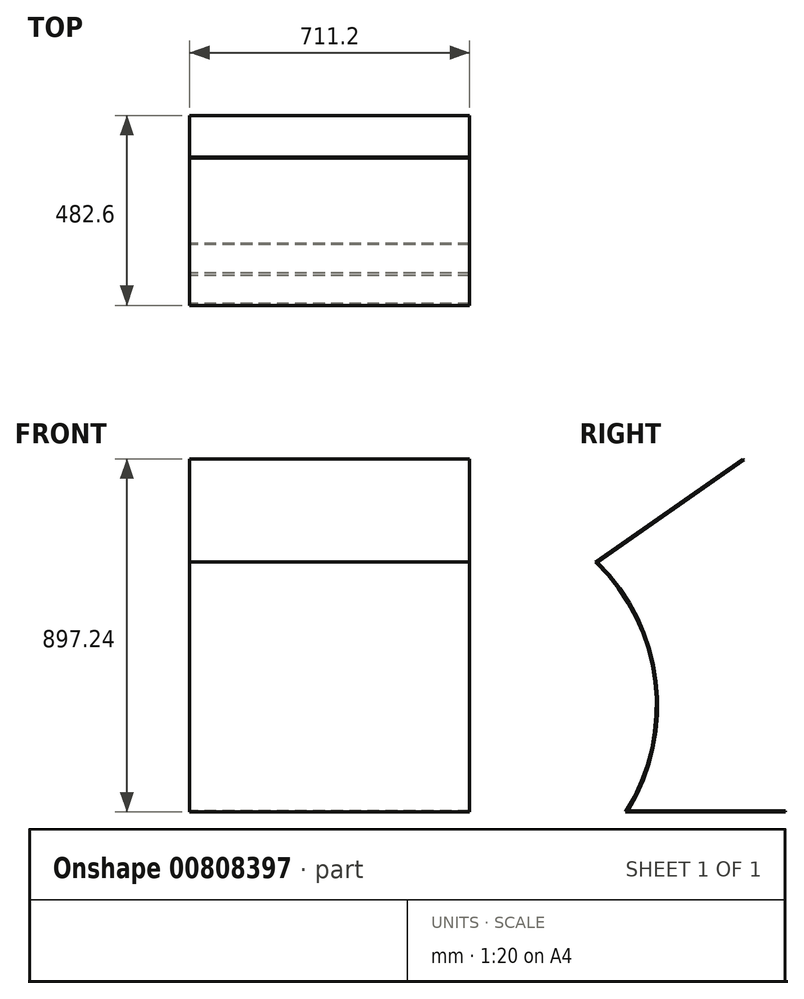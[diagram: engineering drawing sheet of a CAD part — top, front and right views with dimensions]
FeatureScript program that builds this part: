
annotation { "Feature Type Name" : "Feature", "Feature Type Description" : "" }
export const myFeature = defineFeature(function(context is Context, id is Id, definition is map)
    precondition{}
    {
        {
            var Q0;
            Q0=qCreatedBy(makeId("Right.planeOp"),FACE);
            var sketch = newSketch(context, id + "F0", { "sketchPlane" : qUnion([Q0])});
            skLineSegment(sketch, "E0", {"start": v(25.4, 0) * mm, "end": v(-15.24, 0) * mm});
            skArc(sketch, "E1", {"start": v(-15.24, 0) * mm, "mid": v(-7.8, 33.1) * mm, "end": v(-22.86, 63.5) * mm});
            skLineSegment(sketch, "E2", {"start": v(-22.86, 63.5) * mm, "end": v(14.6, 89.72) * mm});
            skLineSegment(sketch, "E3", {"start": v(-22.86, 63.5) * mm, "end": v(22.48, 63.5) * mm, "construction": true});
            skLineSegment(sketch, "E4", {"start": v(0, 0) * mm, "end": v(0, 63.5) * mm, "construction": true});
            skLineSegment(sketch, "E5", {"start": v(-22.86, 63.5) * mm, "end": v(-22.86, 19.24) * mm, "construction": true});
            skLineSegment(sketch, "E6.0", {"start": v(-22.38, 63.46) * mm, "end": v(14.77, 89.47) * mm});
            skArc(sketch, "E6.1", {"start": v(-14.7, 0.3) * mm, "mid": v(-7.51, 33.23) * mm, "end": v(-22.38, 63.46) * mm});
            skLineSegment(sketch, "E6.2", {"start": v(25.4, 0.3) * mm, "end": v(-14.7, 0.3) * mm});
            skLineSegment(sketch, "E7", {"start": v(14.6, 89.72) * mm, "end": v(14.77, 89.47) * mm});
            skLineSegment(sketch, "E8", {"start": v(25.4, 0.3) * mm, "end": v(25.4, 0) * mm});
            skSolve(sketch);
        }
        {
            var Q0;
            Q0 = qSketchRegion(id + "F0", true);
            extrude(context, id + "F1", {"entities" : qUnion([Q0]), "endBound" : BoundingType.SYMMETRIC, "depth" : 71.12 * mm, "offsetDistance" : 25.4 * mm});
        }
        {
            var Q0;
            Q0=makeQuery(id+"F1.opExtrude","SWEPT_BODY",BODY,{"disambiguationData":[OSD([sQuery(id+"F0.wireOp",EDGE,"E0"),sQuery(id+"F0.wireOp",EDGE,"E1"),sQuery(id+"F0.wireOp",EDGE,"E2"),sQuery(id+"F0.wireOp",EDGE,"E6.0"),sQuery(id+"F0.wireOp",EDGE,"E6.1"),sQuery(id+"F0.wireOp",EDGE,"E6.2"),sQuery(id+"F0.wireOp",EDGE,"E7"),sQuery(id+"F0.wireOp",EDGE,"E8")])]});
            var Q1;
            Q1=qCreatedBy(makeId("Origin.pointOp"),VERTEX);
            transform(context, id + "F2", {"entities" : qUnion([Q0]), "transformType" : TransformType.SCALE_UNIFORMLY, "scale" : 10, "scalePoint" : qUnion([Q1]), "makeCopy" : false});
        }
    });
